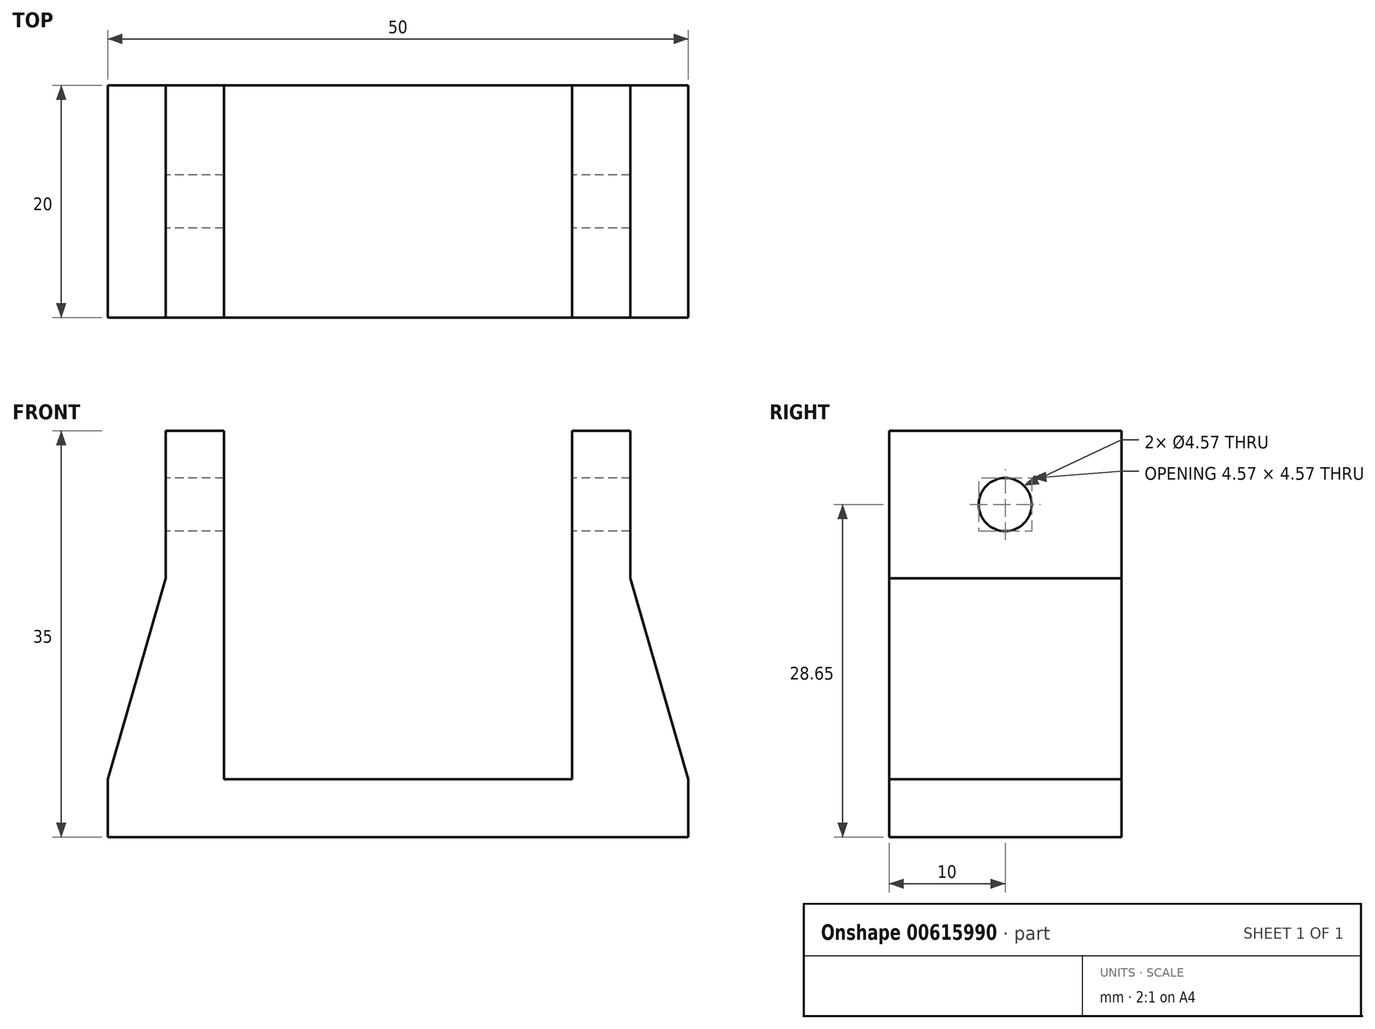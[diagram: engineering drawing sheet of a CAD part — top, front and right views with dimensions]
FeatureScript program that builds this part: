
annotation { "Feature Type Name" : "Feature", "Feature Type Description" : "" }
export const myFeature = defineFeature(function(context is Context, id is Id, definition is map)
    precondition{}
    {
        {
            var Q0;
            Q0=qCreatedBy(makeId("Top.planeOp"),FACE);
            var sketch = newSketch(context, id + "F0", { "sketchPlane" : qUnion([Q0])});
            skLineSegment(sketch, "E0.bottom", {"start": v(25, 10) * mm, "end": v(-25, 10) * mm});
            skLineSegment(sketch, "E0.top", {"start": v(25, -10) * mm, "end": v(-25, -10) * mm});
            skLineSegment(sketch, "E0.left", {"start": v(25, 10) * mm, "end": v(25, -10) * mm});
            skLineSegment(sketch, "E0.right", {"start": v(-25, 10) * mm, "end": v(-25, -10) * mm});
            skPoint(sketch, "E0.middle", {"position": v(0, 0) * mm});
            skSolve(sketch);
        }
        {
            var Q0;
            Q0=makeQuery(id+"F0.imprint","IMPRINT",FACE,{"disambiguationData":[TD([[makeQuery(id+"F0.imprint","IMPRINT",EDGE,{"derivedFrom":sQuery(id+"F0.wireOp",EDGE,"E0.bottom")}),1.0]])]});
            extrude(context, id + "F1", {"entities" : qUnion([Q0]), "depth" : 5 * mm, "offsetDistance" : 25 * mm});
        }
        {
            var Q0;
            Q0=makeQuery(id+"F1.opExtrude","CAP_FACE",FACE,{"disambiguationData":[OSD([sQuery(id+"F0.wireOp",EDGE,"E0.bottom"),sQuery(id+"F0.wireOp",EDGE,"E0.top"),sQuery(id+"F0.wireOp",EDGE,"E0.left"),sQuery(id+"F0.wireOp",EDGE,"E0.right")])],"isStart":false});
            var sketch = newSketch(context, id + "F2", { "sketchPlane" : qUnion([Q0])});
            skLineSegment(sketch, "E1.bottom", {"start": v(25, -10) * mm, "end": v(15, -10) * mm});
            skLineSegment(sketch, "E1.top", {"start": v(25, 10) * mm, "end": v(15, 10) * mm});
            skLineSegment(sketch, "E1.left", {"start": v(25, -10) * mm, "end": v(25, 10) * mm});
            skLineSegment(sketch, "E1.right", {"start": v(15, -10) * mm, "end": v(15, 10) * mm});
            skLineSegment(sketch, "E2.bottom", {"start": v(-25, 10) * mm, "end": v(-15, 10) * mm});
            skLineSegment(sketch, "E2.top", {"start": v(-25, -10) * mm, "end": v(-15, -10) * mm});
            skLineSegment(sketch, "E2.left", {"start": v(-25, 10) * mm, "end": v(-25, -10) * mm});
            skLineSegment(sketch, "E2.right", {"start": v(-15, 10) * mm, "end": v(-15, -10) * mm});
            skSolve(sketch);
        }
        {
            var Q0;
            Q0=qSketchRegion(id+"F2",true);
            extrude(context, id + "F3", {"entities" : qUnion([Q0]), "operationType" : NewBodyOperationType.ADD, "depth" : 30 * mm, "offsetDistance" : 25 * mm});
        }
        {
            var Q0;
            Q0=makeQuery(id+"F3.boolean.opBoolean","MERGE",FACE,{"derivedFrom":[makeQuery(id+"F1.opExtrude","SWEPT_FACE",FACE,{"disambiguationData":[OSD([sQuery(id+"F0.wireOp",EDGE,"E0.bottom")])]}),makeQuery(id+"F3.opExtrude","SWEPT_FACE",FACE,{"disambiguationData":[OSD([sQuery(id+"F2.wireOp",EDGE,"E1.top")])]}),makeQuery(id+"F3.opExtrude","SWEPT_FACE",FACE,{"disambiguationData":[OSD([sQuery(id+"F2.wireOp",EDGE,"E2.bottom")])]})]});
            var sketch = newSketch(context, id + "F4", { "sketchPlane" : qUnion([Q0])});
            skPoint(sketch, "E3", {"position": v(-15, 22.3) * mm});
            skPoint(sketch, "E4", {"position": v(15, 22.3) * mm});
            skLineSegment(sketch, "E5", {"start": v(15, 22.3) * mm, "end": v(15, 35) * mm});
            skLineSegment(sketch, "E6", {"start": v(15, 35) * mm, "end": v(20, 35) * mm});
            skLineSegment(sketch, "E7", {"start": v(20, 35) * mm, "end": v(20, 22.3) * mm});
            skLineSegment(sketch, "E8", {"start": v(20, 22.3) * mm, "end": v(15, 22.3) * mm});
            skLineSegment(sketch, "E9", {"start": v(-15, 22.3) * mm, "end": v(-15, 35) * mm});
            skLineSegment(sketch, "E10", {"start": v(-15, 35) * mm, "end": v(-20, 35) * mm});
            skLineSegment(sketch, "E11", {"start": v(-20, 35) * mm, "end": v(-20, 22.3) * mm});
            skLineSegment(sketch, "E12", {"start": v(-20, 22.3) * mm, "end": v(-15, 22.3) * mm});
            skLineSegment(sketch, "E13", {"start": v(-20, 22.3) * mm, "end": v(-25, 5) * mm});
            skLineSegment(sketch, "E14", {"start": v(20, 22.3) * mm, "end": v(25, 5) * mm});
            skSolve(sketch);
        }
        {
            var Q0;
            {var subQ0=sQuery(id+"F4.wireOp",EDGE,"E11");Q0=makeQuery(id+"F4.imprint","IMPRINT",FACE,{"disambiguationData":[TD([[makeQuery(id+"F4.imprint","IMPRINT",EDGE,{"derivedFrom":subQ0}),-1.0]])]});}
            var Q1;
            {var subQ0=sQuery(id+"F4.wireOp",EDGE,"E7");Q1=makeQuery(id+"F4.imprint","IMPRINT",FACE,{"disambiguationData":[TD([[makeQuery(id+"F4.imprint","IMPRINT",EDGE,{"derivedFrom":subQ0}),1.0]])]});}
            extrude(context, id + "F5", {"entities" : qUnion([Q0, Q1]), "operationType" : NewBodyOperationType.REMOVE, "endBound" : BoundingType.THROUGH_ALL, "oppositeDirection" : true, "depth" : 25 * mm, "offsetDistance" : 25 * mm});
        }
        {
            var Q0;
            Q0=makeQuery(id+"F5.boolean.opBoolean","COPY",FACE,{"derivedFrom":makeQuery(id+"F5.opExtrude","SWEPT_FACE",FACE,{"disambiguationData":[OSD([sQuery(id+"F4.wireOp",EDGE,"E7")])]})});
            var sketch = newSketch(context, id + "F6", { "sketchPlane" : qUnion([Q0])});
            skLineSegment(sketch, "E15", {"start": v(-10, 35) * mm, "end": v(10, 22.3) * mm, "construction": true});
            skLineSegment(sketch, "E16", {"start": v(10, 35) * mm, "end": v(-10, 22.3) * mm, "construction": true});
            skCircle(sketch, "E17", {"center": v(0, 28.65) * mm, "radius": 2.29 * mm});
            skSolve(sketch);
        }
        {
            var Q0;
            Q0=makeQuery(id+"F6.imprint","IMPRINT",FACE,{"disambiguationData":[TD([[makeQuery(id+"F6.imprint","IMPRINT",EDGE,{"derivedFrom":sQuery(id+"F6.wireOp",EDGE,"E17")}),1.0]])]});
            extrude(context, id + "F7", {"entities" : qUnion([Q0]), "operationType" : NewBodyOperationType.REMOVE, "endBound" : BoundingType.THROUGH_ALL, "oppositeDirection" : true, "depth" : 25 * mm, "offsetDistance" : 25 * mm});
        }
    });
